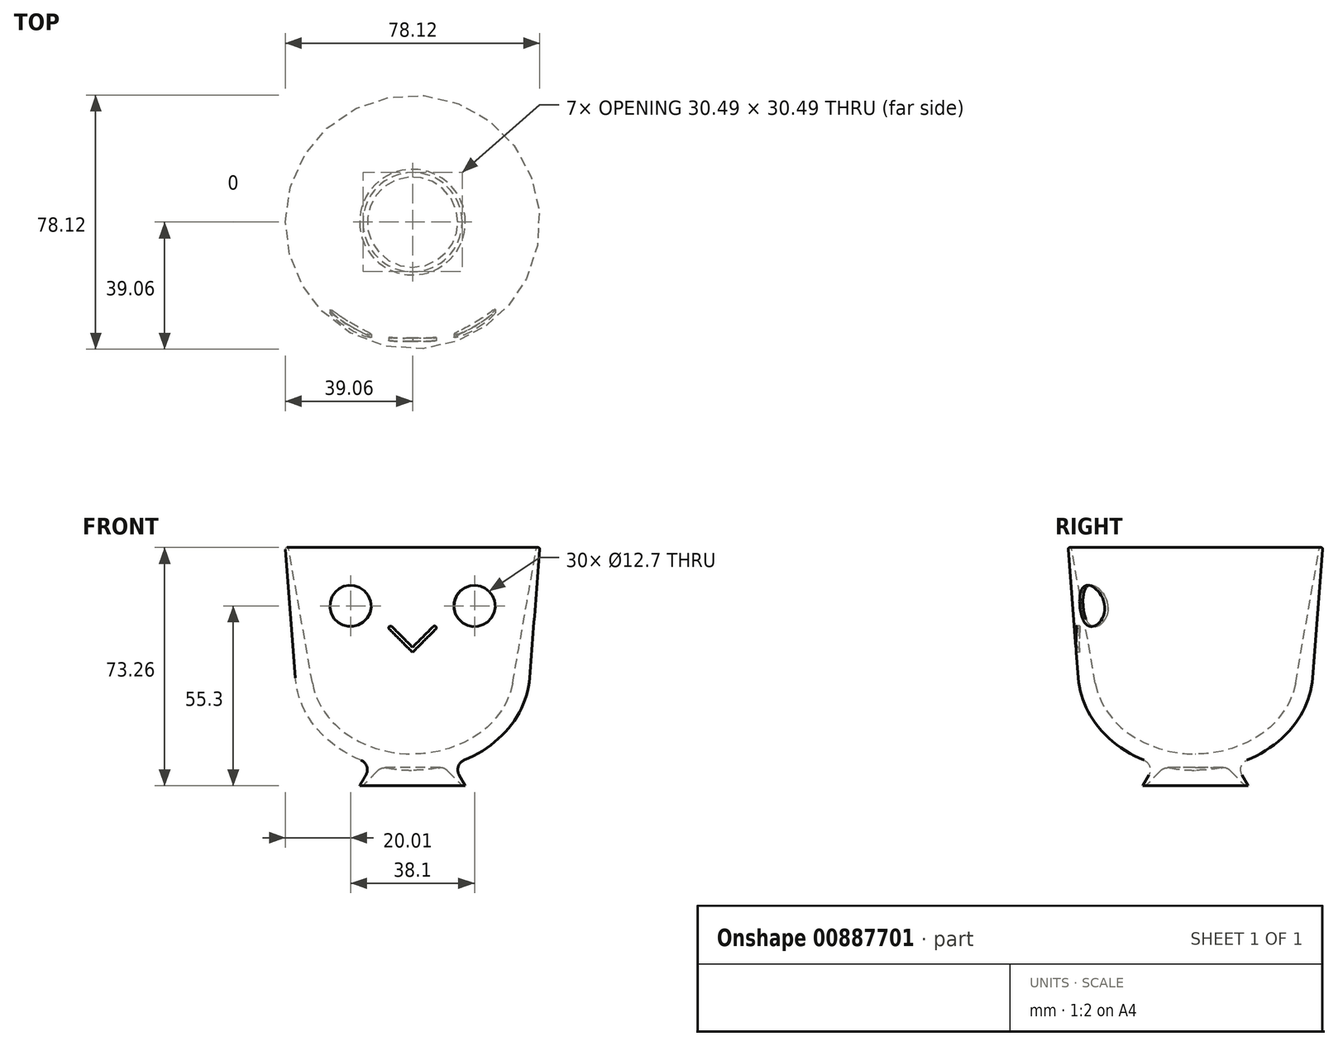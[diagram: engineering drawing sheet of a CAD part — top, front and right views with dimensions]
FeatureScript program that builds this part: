
annotation { "Feature Type Name" : "Feature", "Feature Type Description" : "" }
export const myFeature = defineFeature(function(context is Context, id is Id, definition is map)
    precondition{}
    {
        {
            var Q0;
            Q0=qCreatedBy(makeId("Front.planeOp"),FACE);
            var sketch = newSketch(context, id + "F0", { "sketchPlane" : qUnion([Q0])});
            skEllipse(sketch, "E0", {"center": v(0, -20.14) * mm, "majorRadius": 31.06 * mm, "minorRadius": 25.4 * mm, "majorAxis": v(-1, 0)});
            skLineSegment(sketch, "E1", {"start": v(-30.74, -23.76) * mm, "end": v(-38.1, 17.96) * mm});
            skPoint(sketch, "E2", {"position": v(0, -45.54) * mm});
            skLineSegment(sketch, "E3", {"start": v(-39.1, 17.96) * mm, "end": v(-38.1, 17.96) * mm});
            skLineSegment(sketch, "E4", {"start": v(-39.1, 17.96) * mm, "end": v(-35.74, -25.22) * mm});
            skEllipse(sketch, "E5", {"center": v(0, -20.14) * mm, "majorRadius": 36.06 * mm, "minorRadius": 30.4 * mm, "majorAxis": v(-1, 0)});
            skPoint(sketch, "E6", {"position": v(-36.06, -20.14) * mm});
            skPoint(sketch, "E7", {"position": v(0, -50.54) * mm});
            skPoint(sketch, "E8", {"position": v(-31.06, -20.14) * mm});
            skLineSegment(sketch, "E9", {"start": v(-12.42, -48.68) * mm, "end": v(-16.25, -55.3) * mm});
            skLineSegment(sketch, "E10", {"start": v(-16.25, -55.3) * mm, "end": v(-15.25, -55.3) * mm});
            skLineSegment(sketch, "E11", {"start": v(-15.25, -55.3) * mm, "end": v(-9.53, -49.46) * mm});
            skLineSegment(sketch, "E12", {"start": v(-38.1, 17.96) * mm, "end": v(0, 17.96) * mm});
            skLineSegment(sketch, "E13", {"start": v(0, 17.96) * mm, "end": v(0, -45.54) * mm});
            skLineSegment(sketch, "E14", {"start": v(0, -45.54) * mm, "end": v(0, -50.54) * mm});
            skSolve(sketch);
        }
        {
            var Q0;
            {var subQ0=sQuery(id+"F0.wireOp",EDGE,"E3");Q0=makeQuery(id+"F0.imprint","IMPRINT",FACE,{"disambiguationData":[TD([[makeQuery(id+"F0.imprint","IMPRINT",EDGE,{"derivedFrom":subQ0}),-1.0]])]});}
            var Q1;
            {var subQ8=sQuery(id+"F0.wireOp",EDGE,"E14");Q1=makeQuery(id+"F0.imprint","IMPRINT",FACE,{"disambiguationData":[TD([[makeQuery(id+"F0.imprint","IMPRINT",EDGE,{"derivedFrom":subQ8}),-1.0]])]});}
            var Q2;
            {var subQ0=sQuery(id+"F0.wireOp",EDGE,"E9");Q2=makeQuery(id+"F0.imprint","IMPRINT",FACE,{"disambiguationData":[TD([[makeQuery(id+"F0.imprint","IMPRINT",EDGE,{"derivedFrom":subQ0}),1.0]])]});}
            var Q3;
            Q3=sQuery(id+"F0.wireOp",EDGE,"E13");
            revolve(context, id + "F1", {"surfaceOperationType" : NewSurfaceOperationType.NEW, "entities" : qUnion([Q0, Q1, Q2]), "axis" : qUnion([Q3]), "revolveType" : RevolveType.FULL});
        }
        {
            var Q0;
            Q0=qCreatedBy(makeId("Front.planeOp"),FACE);
            cPlane(context, id + "F2", {"entities" : qUnion([Q0]), "cplaneType" : CPlaneType.OFFSET, "offset" : 38.1 * mm, "width" : 152.4 * mm, "height" : 152.4 * mm});
        }
        {
            var Q0;
            Q0=qCreatedBy(id+"F2.planeOp",FACE);
            var sketch = newSketch(context, id + "F3", { "sketchPlane" : qUnion([Q0])});
            skCircle(sketch, "E15", {"center": v(-19.05, 0) * mm, "radius": 6.35 * mm});
            skCircle(sketch, "E16", {"center": v(19.05, 0) * mm, "radius": 6.35 * mm});
            skLineSegment(sketch, "E17", {"start": v(-6.35, -6.35) * mm, "end": v(0, -12.7) * mm});
            skLineSegment(sketch, "E18", {"start": v(0, -12.7) * mm, "end": v(6.35, -6.35) * mm});
            skPoint(sketch, "E19", {"position": v(19.05, -6.35) * mm});
            skPoint(sketch, "E20", {"position": v(-19.05, -6.35) * mm});
            skLineSegment(sketch, "E21", {"start": v(-7.14, -7.14) * mm, "end": v(0, -14.29) * mm});
            skLineSegment(sketch, "E22", {"start": v(0, -14.29) * mm, "end": v(7.14, -7.14) * mm});
            skArc(sketch, "E23", {"start": v(7.14, -7.14) * mm, "mid": v(7.14, -6.35) * mm, "end": v(6.35, -6.35) * mm});
            skArc(sketch, "E24", {"start": v(-7.14, -7.14) * mm, "mid": v(-7.14, -6.35) * mm, "end": v(-6.35, -6.35) * mm});
            skSolve(sketch);
        }
        {
            var Q0;
            Q0 = qSketchRegion(id + "F3", true);
            var Q1;
            Q1=makeQuery(id+"F1.opRevolve","SWEPT_FACE",FACE,{"disambiguationData":[OSD([sQuery(id+"F0.wireOp",EDGE,"E4")])]});
            extrude(context, id + "F4", {"entities" : qUnion([Q0]), "operationType" : NewBodyOperationType.REMOVE, "endBound" : BoundingType.UP_TO_SURFACE, "oppositeDirection" : true, "depth" : 25.4 * mm, "endBoundEntityFace" : qUnion([Q1]), "hasOffset" : true, "offsetDistance" : 1 * mm, "offsetOppositeDirection" : true});
        }
        {
            var Q0;
            Q0=makeQuery(id+"F1.opRevolve","SWEPT_EDGE",EDGE,{"disambiguationData":[OSD([sQuery(id+"F0.wireOp",EDGE,"E1"),sQuery(id+"F0.wireOp",EDGE,"E3"),sQuery(id+"F0.wireOp",EDGE,"E12")])]});
            var Q1;
            Q1=makeQuery(id+"F1.opRevolve","SWEPT_EDGE",EDGE,{"disambiguationData":[OSD([sQuery(id+"F0.wireOp",EDGE,"E3"),sQuery(id+"F0.wireOp",EDGE,"E4")])]});
            fillet(context, id + "F5", {"entities" : qUnion([Q0, Q1]), "radius" : 0.5 * mm, "tangentPropagation" : true, "allowEdgeOverflow" : false});
        }
        {
            var Q0;
            Q0=makeQuery(id+"F1.opRevolve","SWEPT_EDGE",EDGE,{"disambiguationData":[OSD([sQuery(id+"F0.wireOp",EDGE,"E5"),sQuery(id+"F0.wireOp",EDGE,"E9")])]});
            var Q1;
            Q1=makeQuery(id+"F1.opRevolve","SWEPT_EDGE",EDGE,{"disambiguationData":[OSD([sQuery(id+"F0.wireOp",EDGE,"E5"),sQuery(id+"F0.wireOp",EDGE,"E11")])]});
            fillet(context, id + "F6", {"entities" : qUnion([Q0, Q1]), "radius" : 3.17 * mm, "tangentPropagation" : true, "allowEdgeOverflow" : false});
        }
    });
